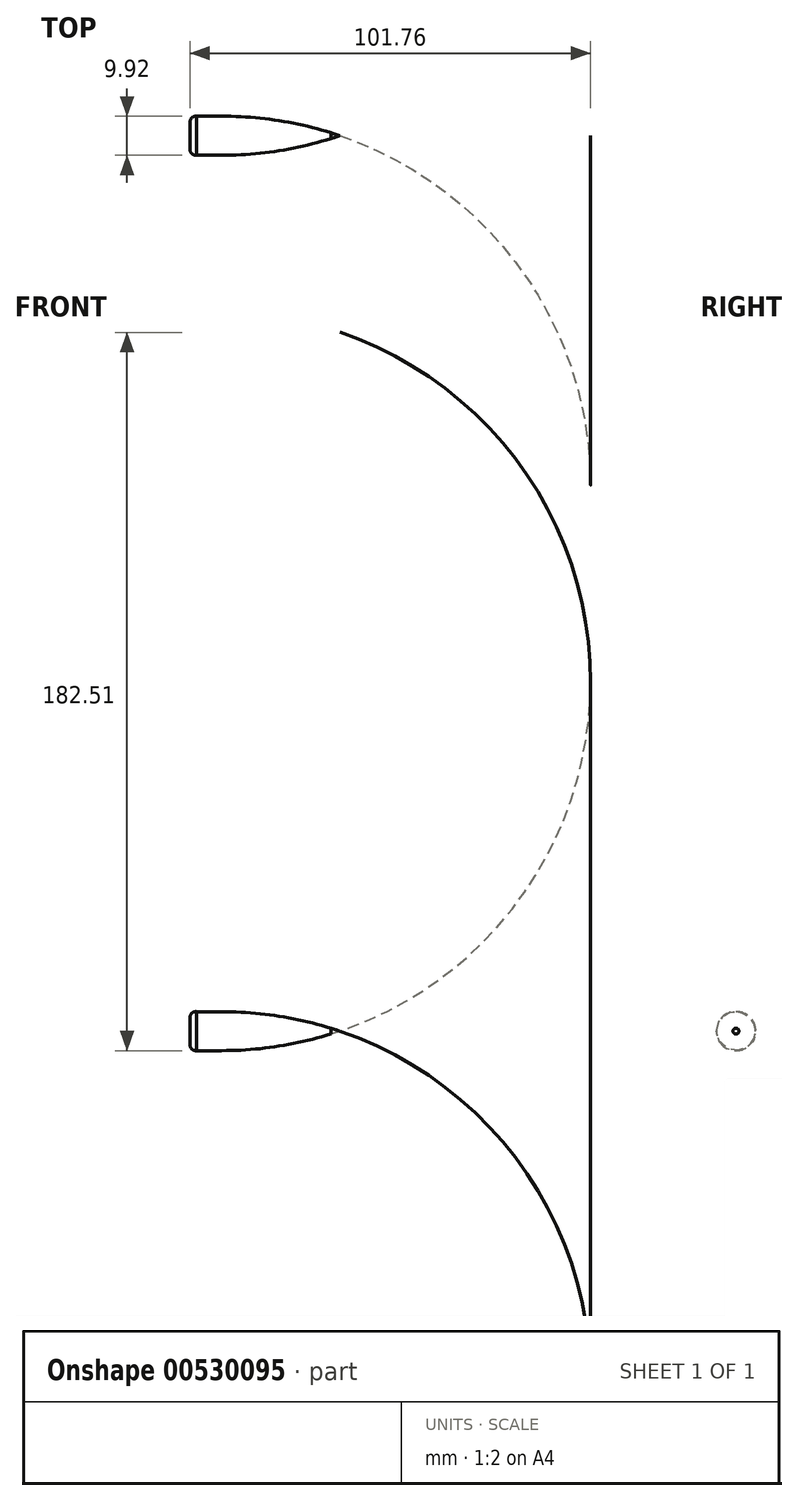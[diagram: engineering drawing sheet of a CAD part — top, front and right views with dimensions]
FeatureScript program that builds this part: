
annotation { "Feature Type Name" : "Feature", "Feature Type Description" : "" }
export const myFeature = defineFeature(function(context is Context, id is Id, definition is map)
    precondition{}
    {
        {
            var Q0;
            Q0=qCreatedBy(makeId("Front.planeOp"),FACE);
            var sketch = newSketch(context, id + "F0", { "sketchPlane" : qUnion([Q0])});
            skLineSegment(sketch, "E0", {"start": v(-16.66, 0) * mm, "end": v(21.44, 0) * mm});
            skLineSegment(sketch, "E1", {"start": v(-16.66, 0) * mm, "end": v(-16.66, 3.45) * mm});
            skArc(sketch, "E2", {"start": v(-14.98, 4.95) * mm, "mid": v(-16.16, 4.58) * mm, "end": v(-16.66, 3.45) * mm});
            skLineSegment(sketch, "E3", {"start": v(-14.98, 4.95) * mm, "end": v(-8.63, 4.95) * mm});
            skArc(sketch, "E4", {"start": v(21.44, 0) * mm, "mid": v(6.6, 3.7) * mm, "end": v(-8.63, 4.95) * mm});
            skLineSegment(sketch, "E5", {"start": v(19.14, 0) * mm, "end": v(19.14, 0.75) * mm});
            skSolve(sketch);
        }
        {
            var Q0;
            {var subQ1=sQuery(id+"F0.wireOp",EDGE,"E1");Q0=makeQuery(id+"F0.imprint","IMPRINT",FACE,{"disambiguationData":[TD([[makeQuery(id+"F0.imprint","IMPRINT",EDGE,{"derivedFrom":subQ1}),-1.0]])]});}
            var Q1;
            Q1=sQuery(id+"F0.wireOp",EDGE,"E0");
            revolve(context, id + "F1", {"entities" : qUnion([Q0]), "axis" : qUnion([Q1]), "revolveType" : RevolveType.FULL});
        }
        {
            var Q0;
            {var subQ3=sQuery(id+"F0.wireOp",EDGE,"E5");Q0=makeQuery(id+"F0.imprint","IMPRINT",FACE,{"disambiguationData":[TD([[makeQuery(id+"F0.imprint","IMPRINT",EDGE,{"derivedFrom":subQ3}),-1.0]])]});}
            var Q1;
            Q1=sQuery(id+"F0.wireOp",EDGE,"E0");
            revolve(context, id + "F2", {"entities" : qUnion([Q0]), "axis" : qUnion([Q1]), "revolveType" : RevolveType.FULL});
        }
    });
